# Revit family: B-3803
name_source: partatom
category: Specialty Equipment
units: mm (PartAtom-declared; Revit-internal decimal feet)

## family parameters
Cut with Voids When Loaded = Yes
Host = Face
OmniClass Number = 23.40.20.21.17
OmniClass Title = Paper Towel Dispensers, Disposal Units
Part Type = Normal
Room Calculation Point = No
Round Connector Dimension = Use Diameter
Shared = Yes

## types (1)
- B-3803
    Assembly Code = C1030200
    Default Elevation = 37 3/8"
    Description = TrimLineSeries Recessed Paper Towel Dispenser And Waste Receptacle
    Finish = Stainless Steel-Bobrick-Satin
    Height = 55 1/8"
    Length = 5 5/8"
    Manufacturer = Bobrick
    Material = Stainless Steel-Bobrick-Satin
    Model = B-3803
    Product Documentation Link = https://www.bobrick.com
    Product Page URL = https://www.bobrick.com
    Revised Date = 11/05/2020
    URL = http://www.bobrick.com
    Width = 13"

## geometry (parser evidence)
native form markers: Sweep x3
no freeform markers — native parametric forms only
